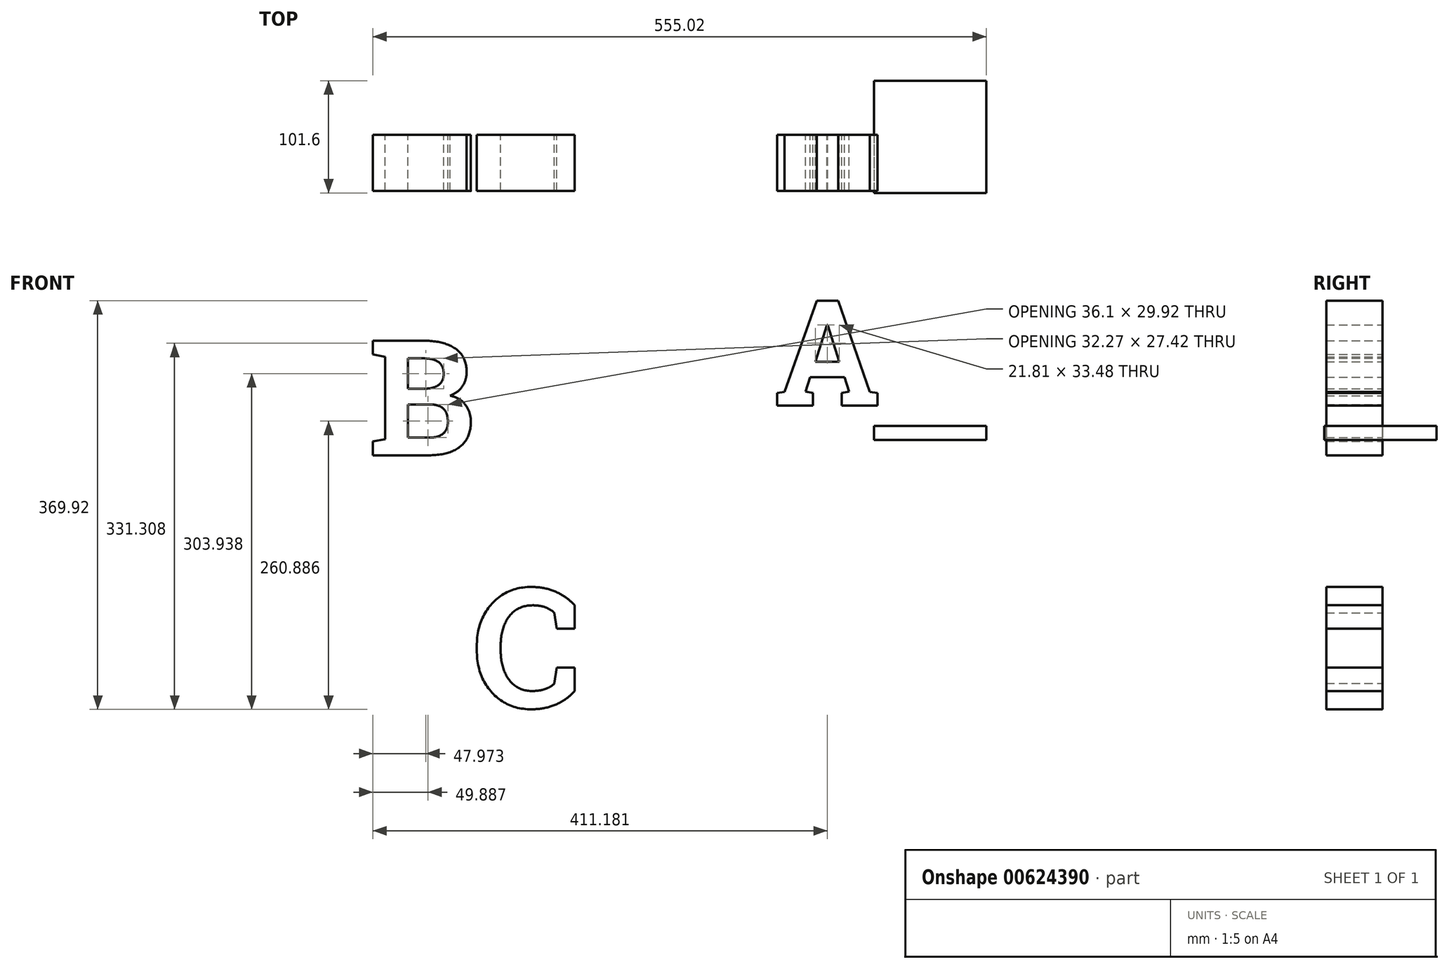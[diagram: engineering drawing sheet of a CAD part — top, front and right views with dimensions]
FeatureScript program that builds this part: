
annotation { "Feature Type Name" : "Feature", "Feature Type Description" : "" }
export const myFeature = defineFeature(function(context is Context, id is Id, definition is map)
    precondition{}
    {
        {
            var Q0;
            Q0=qCreatedBy(makeId("Top.planeOp"),FACE);
            var sketch = newSketch(context, id + "F0", { "sketchPlane" : qUnion([Q0])});
            skLineSegment(sketch, "E0.bottom", {"start": v(-24.29, 49) * mm, "end": v(77.31, 49) * mm});
            skLineSegment(sketch, "E0.top", {"start": v(-24.29, -52.6) * mm, "end": v(77.31, -52.6) * mm});
            skLineSegment(sketch, "E0.left", {"start": v(-24.29, 49) * mm, "end": v(-24.29, -52.6) * mm});
            skLineSegment(sketch, "E0.right", {"start": v(77.31, 49) * mm, "end": v(77.31, -52.6) * mm});
            skSolve(sketch);
        }
        {
            var Q0;
            Q0 = qSketchRegion(id + "F0", true);
            extrude(context, id + "F1", {"entities" : qUnion([Q0]), "endBound" : BoundingType.SYMMETRIC, "depth" : 12.7 * mm, "offsetDistance" : 25.4 * mm});
        }
        {
            var Q0;
            Q0=qCreatedBy(makeId("Front.planeOp"),FACE);
            var sketch = newSketch(context, id + "F2", { "sketchPlane" : qUnion([Q0])});
            skText(sketch, "E1", { "text": "A", "fontName": "RobotoSlab-Bold.ttf"});
            const initialGuessF2  = {"E1": [-0.11457, 0.02477, 1, 0, 0.09625]};
            skSetInitialGuess(sketch, initialGuessF2);
            skSolve(sketch);
        }
        {
            var Q0;
            Q0 = qSketchRegion(id + "F2", true);
            extrude(context, id + "F3", {"entities" : qUnion([Q0]), "depth" : 50.8 * mm, "offsetDistance" : 25.4 * mm});
        }
        {
            var Q0;
            Q0=qCreatedBy(makeId("Front.planeOp"),FACE);
            var sketch = newSketch(context, id + "F4", { "sketchPlane" : qUnion([Q0])});
            skText(sketch, "E2", { "text": "B", "fontName": "RobotoSlab-Bold.ttf"});
            const initialGuessF4  = {"E2": [-0.4817, -0.02014, 1, 0, 0.10502]};
            skSetInitialGuess(sketch, initialGuessF4);
            skSolve(sketch);
        }
        {
            var Q0;
            Q0 = qSketchRegion(id + "F4", true);
            extrude(context, id + "F5", {"entities" : qUnion([Q0]), "depth" : 50.8 * mm, "offsetDistance" : 25.4 * mm});
        }
        {
            var Q0;
            Q0=qCreatedBy(makeId("Front.planeOp"),FACE);
            var sketch = newSketch(context, id + "F6", { "sketchPlane" : qUnion([Q0])});
            skText(sketch, "E3", { "text": "C", "fontName": "RobotoSlab-Bold.ttf"});
            const initialGuessF6  = {"E3": [-0.38748, -0.24855, 1, 0, 0.109]};
            skSetInitialGuess(sketch, initialGuessF6);
            skSolve(sketch);
        }
        {
            var Q0;
            Q0 = qSketchRegion(id + "F6", true);
            extrude(context, id + "F7", {"entities" : qUnion([Q0]), "depth" : 50.8 * mm, "offsetDistance" : 25.4 * mm});
        }
    });
